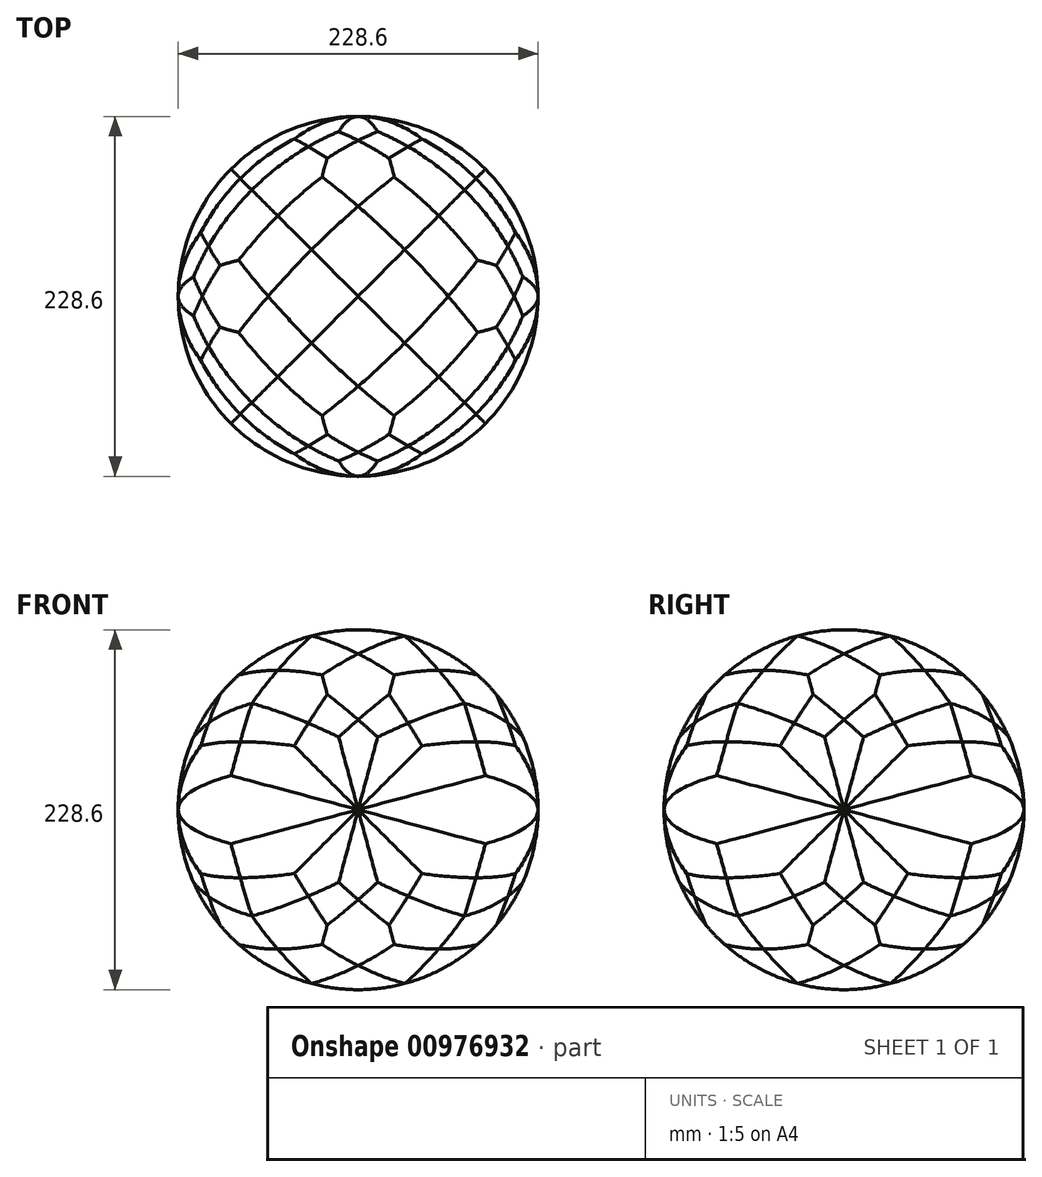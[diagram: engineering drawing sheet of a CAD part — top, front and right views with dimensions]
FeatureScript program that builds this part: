
annotation { "Feature Type Name" : "Feature", "Feature Type Description" : "" }
export const myFeature = defineFeature(function(context is Context, id is Id, definition is map)
    precondition{}
    {
        {
            var Q0;
            Q0=qCreatedBy(makeId("Top.planeOp"),FACE);
            var sketch = newSketch(context, id + "F0", { "sketchPlane" : qUnion([Q0])});
            skCircle(sketch, "E0", {"center": v(0, 0) * mm, "radius": 114.3 * mm});
            skLineSegment(sketch, "E1", {"start": v(0, -114.3) * mm, "end": v(0, 114.3) * mm, "construction": true});
            skLineSegment(sketch, "E2", {"start": v(-114.3, 0) * mm, "end": v(114.3, 0) * mm, "construction": true});
            skSolve(sketch);
        }
        {
            var Q0;
            Q0=makeQuery(id+"F0.imprint","IMPRINT",FACE,{"disambiguationData":[TD([[makeQuery(id+"F0.imprint","IMPRINT",EDGE,{"derivedFrom":sQuery(id+"F0.wireOp",EDGE,"E0")}),1.0]])]});
            extrude(context, id + "F1", {"entities" : qUnion([Q0]), "endBound" : BoundingType.SYMMETRIC, "depth" : 76200 * mm, "offsetDistance" : 25.4 * mm});
        }
        {
            var Q0;
            Q0=makeQuery(id+"F1.opExtrude","SWEPT_BODY",BODY,{"disambiguationData":[OSD([sQuery(id+"F0.wireOp",EDGE,"E0")])]});
            var Q1;
            Q1=sQuery(id+"F0.wireOp",EDGE,"E1");
            circularPattern(context, id + "F2", {"entities" : qUnion([Q0]), "axis" : qUnion([Q1]), "angle" : 30 * degree, "instanceCount" : 16});
        }
        {
            var Q0;
            Q0=makeQuery(id+"F1.opExtrude","SWEPT_BODY",BODY,{"disambiguationData":[OSD([sQuery(id+"F0.wireOp",EDGE,"E0")])]});
            var Q1;
            Q1=sQuery(id+"F0.wireOp",EDGE,"E2");
            circularPattern(context, id + "F3", {"entities" : qUnion([Q0]), "axis" : qUnion([Q1]), "angle" : 30 * degree, "instanceCount" : 16});
        }
        {
            var Q0;
            Q0=makeQuery(id+"F2.opPattern","COPY",BODY,{"derivedFrom":makeQuery(id+"F1.opExtrude","SWEPT_BODY",BODY,{"disambiguationData":[OSD([sQuery(id+"F0.wireOp",EDGE,"E0")])]}),"instanceName":"1"});
            var Q1;
            Q1=makeQuery(id+"F1.opExtrude","SWEPT_BODY",BODY,{"disambiguationData":[OSD([sQuery(id+"F0.wireOp",EDGE,"E0")])]});
            var Q2;
            Q2=makeQuery(id+"F3.opPattern","COPY",BODY,{"derivedFrom":makeQuery(id+"F1.opExtrude","SWEPT_BODY",BODY,{"disambiguationData":[OSD([sQuery(id+"F0.wireOp",EDGE,"E0")])]}),"instanceName":"1"});
            var Q3;
            Q3=makeQuery(id+"F2.opPattern","COPY",BODY,{"derivedFrom":makeQuery(id+"F1.opExtrude","SWEPT_BODY",BODY,{"disambiguationData":[OSD([sQuery(id+"F0.wireOp",EDGE,"E0")])]}),"instanceName":"2"});
            var Q4;
            Q4=makeQuery(id+"F2.opPattern","COPY",BODY,{"derivedFrom":makeQuery(id+"F1.opExtrude","SWEPT_BODY",BODY,{"disambiguationData":[OSD([sQuery(id+"F0.wireOp",EDGE,"E0")])]}),"instanceName":"5"});
            var Q5;
            Q5=makeQuery(id+"F2.opPattern","COPY",BODY,{"derivedFrom":makeQuery(id+"F1.opExtrude","SWEPT_BODY",BODY,{"disambiguationData":[OSD([sQuery(id+"F0.wireOp",EDGE,"E0")])]}),"instanceName":"4"});
            var Q6;
            Q6=makeQuery(id+"F3.opPattern","COPY",BODY,{"derivedFrom":makeQuery(id+"F1.opExtrude","SWEPT_BODY",BODY,{"disambiguationData":[OSD([sQuery(id+"F0.wireOp",EDGE,"E0")])]}),"instanceName":"2"});
            var Q7;
            Q7=makeQuery(id+"F3.opPattern","COPY",BODY,{"derivedFrom":makeQuery(id+"F1.opExtrude","SWEPT_BODY",BODY,{"disambiguationData":[OSD([sQuery(id+"F0.wireOp",EDGE,"E0")])]}),"instanceName":"4"});
            var Q8;
            Q8=makeQuery(id+"F2.opPattern","COPY",BODY,{"derivedFrom":makeQuery(id+"F1.opExtrude","SWEPT_BODY",BODY,{"disambiguationData":[OSD([sQuery(id+"F0.wireOp",EDGE,"E0")])]}),"instanceName":"7"});
            var Q9;
            Q9=makeQuery(id+"F3.opPattern","COPY",BODY,{"derivedFrom":makeQuery(id+"F1.opExtrude","SWEPT_BODY",BODY,{"disambiguationData":[OSD([sQuery(id+"F0.wireOp",EDGE,"E0")])]}),"instanceName":"3"});
            var Q10;
            Q10=makeQuery(id+"F3.opPattern","COPY",BODY,{"derivedFrom":makeQuery(id+"F1.opExtrude","SWEPT_BODY",BODY,{"disambiguationData":[OSD([sQuery(id+"F0.wireOp",EDGE,"E0")])]}),"instanceName":"5"});
            var Q11;
            Q11=makeQuery(id+"F3.opPattern","COPY",BODY,{"derivedFrom":makeQuery(id+"F1.opExtrude","SWEPT_BODY",BODY,{"disambiguationData":[OSD([sQuery(id+"F0.wireOp",EDGE,"E0")])]}),"instanceName":"7"});
            var Q12;
            Q12=makeQuery(id+"F3.opPattern","COPY",BODY,{"derivedFrom":makeQuery(id+"F1.opExtrude","SWEPT_BODY",BODY,{"disambiguationData":[OSD([sQuery(id+"F0.wireOp",EDGE,"E0")])]}),"instanceName":"6"});
            var Q13;
            Q13=makeQuery(id+"F2.opPattern","COPY",BODY,{"derivedFrom":makeQuery(id+"F1.opExtrude","SWEPT_BODY",BODY,{"disambiguationData":[OSD([sQuery(id+"F0.wireOp",EDGE,"E0")])]}),"instanceName":"6"});
            var Q14;
            Q14=makeQuery(id+"F2.opPattern","COPY",BODY,{"derivedFrom":makeQuery(id+"F1.opExtrude","SWEPT_BODY",BODY,{"disambiguationData":[OSD([sQuery(id+"F0.wireOp",EDGE,"E0")])]}),"instanceName":"3"});
            var Q15;
            Q15=makeQuery(id+"F2.opPattern","COPY",BODY,{"derivedFrom":makeQuery(id+"F1.opExtrude","SWEPT_BODY",BODY,{"disambiguationData":[OSD([sQuery(id+"F0.wireOp",EDGE,"E0")])]}),"instanceName":"8"});
            var Q16;
            Q16=makeQuery(id+"F2.opPattern","COPY",BODY,{"derivedFrom":makeQuery(id+"F1.opExtrude","SWEPT_BODY",BODY,{"disambiguationData":[OSD([sQuery(id+"F0.wireOp",EDGE,"E0")])]}),"instanceName":"9"});
            var Q17;
            Q17=makeQuery(id+"F2.opPattern","COPY",BODY,{"derivedFrom":makeQuery(id+"F1.opExtrude","SWEPT_BODY",BODY,{"disambiguationData":[OSD([sQuery(id+"F0.wireOp",EDGE,"E0")])]}),"instanceName":"11"});
            var Q18;
            Q18=makeQuery(id+"F2.opPattern","COPY",BODY,{"derivedFrom":makeQuery(id+"F1.opExtrude","SWEPT_BODY",BODY,{"disambiguationData":[OSD([sQuery(id+"F0.wireOp",EDGE,"E0")])]}),"instanceName":"12"});
            var Q19;
            Q19=makeQuery(id+"F2.opPattern","COPY",BODY,{"derivedFrom":makeQuery(id+"F1.opExtrude","SWEPT_BODY",BODY,{"disambiguationData":[OSD([sQuery(id+"F0.wireOp",EDGE,"E0")])]}),"instanceName":"15"});
            var Q20;
            Q20=makeQuery(id+"F2.opPattern","COPY",BODY,{"derivedFrom":makeQuery(id+"F1.opExtrude","SWEPT_BODY",BODY,{"disambiguationData":[OSD([sQuery(id+"F0.wireOp",EDGE,"E0")])]}),"instanceName":"10"});
            var Q21;
            Q21=makeQuery(id+"F2.opPattern","COPY",BODY,{"derivedFrom":makeQuery(id+"F1.opExtrude","SWEPT_BODY",BODY,{"disambiguationData":[OSD([sQuery(id+"F0.wireOp",EDGE,"E0")])]}),"instanceName":"14"});
            var Q22;
            Q22=makeQuery(id+"F3.opPattern","COPY",BODY,{"derivedFrom":makeQuery(id+"F1.opExtrude","SWEPT_BODY",BODY,{"disambiguationData":[OSD([sQuery(id+"F0.wireOp",EDGE,"E0")])]}),"instanceName":"13"});
            var Q23;
            Q23=makeQuery(id+"F3.opPattern","COPY",BODY,{"derivedFrom":makeQuery(id+"F1.opExtrude","SWEPT_BODY",BODY,{"disambiguationData":[OSD([sQuery(id+"F0.wireOp",EDGE,"E0")])]}),"instanceName":"11"});
            var Q24;
            Q24=makeQuery(id+"F3.opPattern","COPY",BODY,{"derivedFrom":makeQuery(id+"F1.opExtrude","SWEPT_BODY",BODY,{"disambiguationData":[OSD([sQuery(id+"F0.wireOp",EDGE,"E0")])]}),"instanceName":"10"});
            var Q25;
            Q25=makeQuery(id+"F2.opPattern","COPY",BODY,{"derivedFrom":makeQuery(id+"F1.opExtrude","SWEPT_BODY",BODY,{"disambiguationData":[OSD([sQuery(id+"F0.wireOp",EDGE,"E0")])]}),"instanceName":"13"});
            var Q26;
            Q26=makeQuery(id+"F3.opPattern","COPY",BODY,{"derivedFrom":makeQuery(id+"F1.opExtrude","SWEPT_BODY",BODY,{"disambiguationData":[OSD([sQuery(id+"F0.wireOp",EDGE,"E0")])]}),"instanceName":"15"});
            var Q27;
            Q27=makeQuery(id+"F3.opPattern","COPY",BODY,{"derivedFrom":makeQuery(id+"F1.opExtrude","SWEPT_BODY",BODY,{"disambiguationData":[OSD([sQuery(id+"F0.wireOp",EDGE,"E0")])]}),"instanceName":"12"});
            var Q28;
            Q28=makeQuery(id+"F3.opPattern","COPY",BODY,{"derivedFrom":makeQuery(id+"F1.opExtrude","SWEPT_BODY",BODY,{"disambiguationData":[OSD([sQuery(id+"F0.wireOp",EDGE,"E0")])]}),"instanceName":"8"});
            var Q29;
            Q29=makeQuery(id+"F3.opPattern","COPY",BODY,{"derivedFrom":makeQuery(id+"F1.opExtrude","SWEPT_BODY",BODY,{"disambiguationData":[OSD([sQuery(id+"F0.wireOp",EDGE,"E0")])]}),"instanceName":"14"});
            var Q30;
            Q30=makeQuery(id+"F3.opPattern","COPY",BODY,{"derivedFrom":makeQuery(id+"F1.opExtrude","SWEPT_BODY",BODY,{"disambiguationData":[OSD([sQuery(id+"F0.wireOp",EDGE,"E0")])]}),"instanceName":"9"});
            booleanBodies(context, id + "F4", {"operationType" : BooleanOperationType.INTERSECTION, "tools" : qUnion([Q0, Q1, Q2, Q3, Q4, Q5, Q6, Q7, Q8, Q9, Q10, Q11, Q12, Q13, Q14, Q15, Q16, Q17, Q18, Q19, Q20, Q21, Q22, Q23, Q24, Q25, Q26, Q27, Q28, Q29, Q30])});
        }
    });
